# Revit family: 04780200
name_source: partatom
category: Plumbing Fixtures
revit_build: Autodesk Revit 2018 (Build: 20170223_1515(x64)
units: mm (PartAtom-declared; Revit-internal decimal feet)

## family parameters
Always vertical = Yes
Cut with Voids When Loaded = No
OmniClass Number = 23.45.55.00
OmniClass Title = Sanitary Faucets, Wastes
Part Type = Normal
Room Calculation Point = No
Round Connector Dimension = Use Diameter
Shared = No
Work Plane-Based = No

## types (1)
- 04780200 Shower rail
    2D/3D/BIM Files URL = http://static.hansa.com
    3D View = https://static.hansa.com
    Advanced Features = Flexible length / can be shortened
    AssetType = Fixed
    BIMObjectName = 04780200
    BodyMaterial = Brass
    Brand = HANSA
    Catalog Drawing URL = http://static.hansa.com
    Category = Bathroom;Shower
    CloseOffRating = 0
    Color = Chrome
    DN Size = 22 mm
    Diameter = 22 mm
    DurationUnit = Year
    EAN Number = 4057304008672
    ETIM Class Number = EC010140 Sliding rod
    FDV Document URL = http://www.hansa.com
    FaucetMainMaterial = Brass
    Finish = Polished
    FlowCoefficient = 0
    Group = Shower rail
    IfcExportAs = IfcValveType
    IfcExportType = FAUCET
    Installation Type = Wall mounted
    Installation and Maintenance Guide URL = http://static.hansa.com
    Interactive AR View URL = https://static.hansa.com
    Manufacturer = HANSA
    ManufacturerName = HANSA
    ManufacturerURL = http://www.hansa.com
    Market = International;Germany;Austria;Belgium;Netherlands;France;Czech Republic;Slovakia;Italy;Spain
    Material = Brass
    Mechanical Parts = Fixing Set
    Mobile Product Information URL = http://mpi.hansa.com
    Model = 04780200 Shower rail
    ModelReference = 04780200
    NBSDescription = Shower mixers
    NBSReference = 45-35-70/335
    Name = 04780200 Shower rail
    Name_en = 04780200 Shower rail
    NominalDepth = 103 mm
    NominalHeight = 760 mm
    NominalWidth = 67 mm
    Product Code = 04780200
    Product Family = HANSAACTIVEJET
    Product Image URL = http://static.hansa.com
    Product URL = http://static.hansa.com
    Revision = 2
    Sales Package dimensions (LxWxH) = 1031 x 156 x 74
    Shape = Sculptured
    Shower Parts = Shower rail;Variable fixing points;Adjustable shower rail bracket
    Size = 65x105x760 mm
    Spare-Part Information URL = http://static.hansa.com
    Surface treatment = Chrome
    Technical DataSheet URL = http://www.hansa.com
    UNSPSC Class Number = 30181503 Showers
    URL Declaration of Conformity = http://static.hansa.com
    URL REACH = http://static.hansa.com
    Uniclass2 = Pr_40_30_96_78
    Uniclass2015Description = Shower manual water supply sets
    Uniclass2015Reference = Pr_40_20_87_78
    Version = 2
    VersionDate = 01/07/2022
    Warranty Information URL = http://warranty.hansa.com
    WarrantyDescription = http://warranty.hansa.com
    WarrantyDurationUnit = Year

## geometry (parser evidence)
native form markers: Sweep x6
no freeform markers — native parametric forms only
